SOLIDWORKS PART (.sldprt)
format: sldprt  version: not decoded by parser v0  size: 171,520 bytes
history: native  units: mm
features: plane x3, sketch x3, extrude x2, material x1, cut_extrude x1 (+13 scaffold rows collapsed)
feature tree (23):
  scaffold x13  (default folders/planes/origin — collapsed)
  material  "材质 <未指定>"
  plane  "前视基准面"
  plane  "上视基准面"
  plane  "右视基准面"
  sketch  "草图1"  dims[D1=88.0mm D2=35.0mm]
  extrude  "凸台-拉伸1"  Depth=4mm
  sketch  "草图2"  dims[D1=9.0mm D2=39.0mm D3=9.0mm D4=39.0mm]
  cut_extrude  "切除-拉伸1"  [1 undecoded]
  sketch  "草图3"  dims[c1.D1=~12.005286mm c2.D1=120.0deg c2.D2=~12.186969mm c3.D2=150.0deg c3.D3=12.0mm c3.D4=10.0mm c3.D5=15.0mm]
  extrude  "凸台-拉伸2"  Depth=25mm
decode coverage: 5 of 6 modeling features carry decoded parameters
note: ~ marks probable driven/reference dimensions
note: 1 parameter value undecoded
note: suppression state not decoded; provenance and decode notes live in map.json
